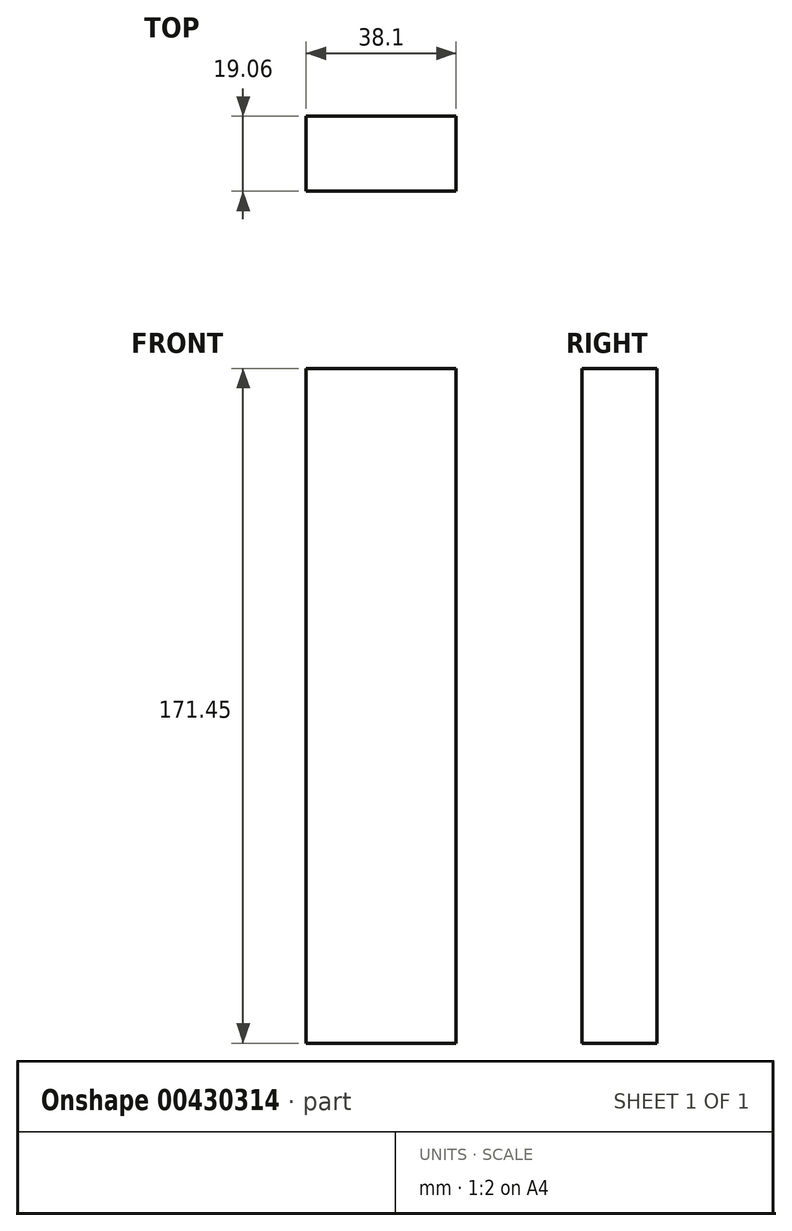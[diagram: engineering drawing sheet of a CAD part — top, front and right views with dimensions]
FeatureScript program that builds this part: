
annotation { "Feature Type Name" : "Feature", "Feature Type Description" : "" }
export const myFeature = defineFeature(function(context is Context, id is Id, definition is map)
    precondition{}
    {
        {
            var Q0;
            Q0=qCreatedBy(makeId("Top.planeOp"),FACE);
            var sketch = newSketch(context, id + "F0", { "sketchPlane" : qUnion([Q0])});
            skLineSegment(sketch, "E0.bottom", {"start": v(19.05, 9.53) * mm, "end": v(-19.05, 9.53) * mm});
            skLineSegment(sketch, "E0.top", {"start": v(19.05, -9.53) * mm, "end": v(-19.05, -9.53) * mm});
            skLineSegment(sketch, "E0.left", {"start": v(19.05, 9.53) * mm, "end": v(19.05, -9.53) * mm});
            skLineSegment(sketch, "E0.right", {"start": v(-19.05, 9.53) * mm, "end": v(-19.05, -9.53) * mm});
            skPoint(sketch, "E0.middle", {"position": v(0, 0) * mm});
            skSolve(sketch);
        }
        {
            var Q0;
            Q0=qSketchRegion(id+"F0",true);
            extrude(context, id + "F1", {"entities" : qUnion([Q0]), "depth" : 171.45 * mm});
        }
    });
